# Revit family: Cleanout_Square_Industrial_Floor-Zurn-Z1840-8S
name_source: partatom
category: Plumbing Fixtures
units: mm (PartAtom-declared; Revit-internal decimal feet)

## family parameters
Always vertical = Yes
Cut with Voids When Loaded = No
Maintain Annotation Orientation = No
OmniClass Number = 23.45.55.21
OmniClass Title = Drains (Wastes)
Part Type = Normal
Room Calculation Point = No
Round Connector Dimension = Use Radius
Shared = No
Work Plane-Based = No

## types (1)
- Load Family Type Catalog
    Assembly Code = D2030300
    CW Connection = No
    CWFU = 0
    Default Elevation = 20 "
    Description = 8” x 8” [203 x 203] SQUARE INDUSTRIAL FLOOR CLEANOUT
    Drain Total Height = 5.5 "
    Grate Thickness = 0.563 "
    HW Connection = No
    HWFU = 0
    Main Material = Steel - Zurn- Stainless - Type - 316
    Manufacturer = Zurn Water, LLC
    Manufacurer Brand = Zurn
    Model = ZM1840-8S
    Modified Date = 02/27/26
    Pipe Size 'A' (Inner Diameter) = 6.357 "
    Pipe Size 'A' (Inner Radius) = 3.179 "
    Pipe Size 'A' (Nominal Diameter) = 6 "
    Pipe Size 'A' (Nominal Radius) = 3 "
    Pipe Size 'A' (Outer Diameter) = 6.625 "
    Pipe Size 'A' (Outer Radius) = 3.313 "
    Product Documentation Link = https://files.zurn.com
    Product Page URL = https://www.zurn.com
    Square Drain Dimension = 8.218 "
    Type Comments = ZM1840-8S_6 Inch No-Hub Outlet (Sch. 10)
    URL = www.zurn.com
    Vent Connection = No
    WFU = 1
    Waste Connection = Yes

## geometry (parser evidence)
native form markers: Sweep x3
no freeform markers — native parametric forms only
